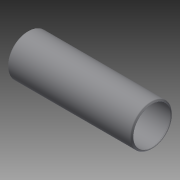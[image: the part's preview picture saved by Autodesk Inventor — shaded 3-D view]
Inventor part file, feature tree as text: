
AUTODESK INVENTOR PART (.ipt)
format: ipt  version: 2014 SP2 (Build 180246200, 246)  size: 146,944 bytes
history: native  units: in
note: dims shown in document units (in); Inventor stores cm internally (conversion verified against a paired STEP export)
features: other x42, revolve x1, sketch x1
ambient origin geometry x8: Origin, YZ Plane, XZ Plane, XY Plane, X Axis, Y Axis, Z Axis, Center Point
bodies: Solid1 (feature_tree)
feature tree (44):
  revolve  "Revolution1"  [1 undecoded]
  other  "cp1_XY"
  other  "cp1_YZ"
  other  "cp1_ZX"
  other  "cp1_X"
  other  "cp1_Y"
  other  "cp1_Z"
  other  "cp1_Center"
  other  "cp2_XY"
  other  "cp2_YZ"
  other  "cp2_ZX"
  other  "cp2_X"
  other  "cp2_Y"
  other  "cp2_Z"
  other  "cp2_Center"
  other  "cp3_XY"
  other  "cp3_YZ"
  other  "cp3_ZX"
  other  "cp3_X"
  other  "cp3_Y"
  other  "cp3_Z"
  other  "cp3_Center"
  other  "cp4_XY"
  other  "cp4_YZ"
  other  "cp4_ZX"
  other  "cp4_X"
  other  "cp4_Y"
  other  "cp4_Z"
  other  "cp4_Center"
  other  "tube_front_XY"
  other  "tube_front_YZ"
  other  "tube_front_ZX"
  other  "tube_front_X"
  other  "tube_front_Y"
  other  "tube_front_Z"
  other  "tube_front_Center"
  other  "tube_rear_XY"
  other  "tube_rear_YZ"
  other  "tube_rear_ZX"
  other  "tube_rear_X"
  other  "tube_rear_Y"
  other  "tube_rear_Z"
  other  "tube_rear_Center"
  sketch  "Sketch_1"  dims[d0=360.0deg]
note: 1 required parameter value undecoded (feature->parameter linkage not recoverable at this tier; creation-order binding heuristic only, values carry confidence <= 0.55)
